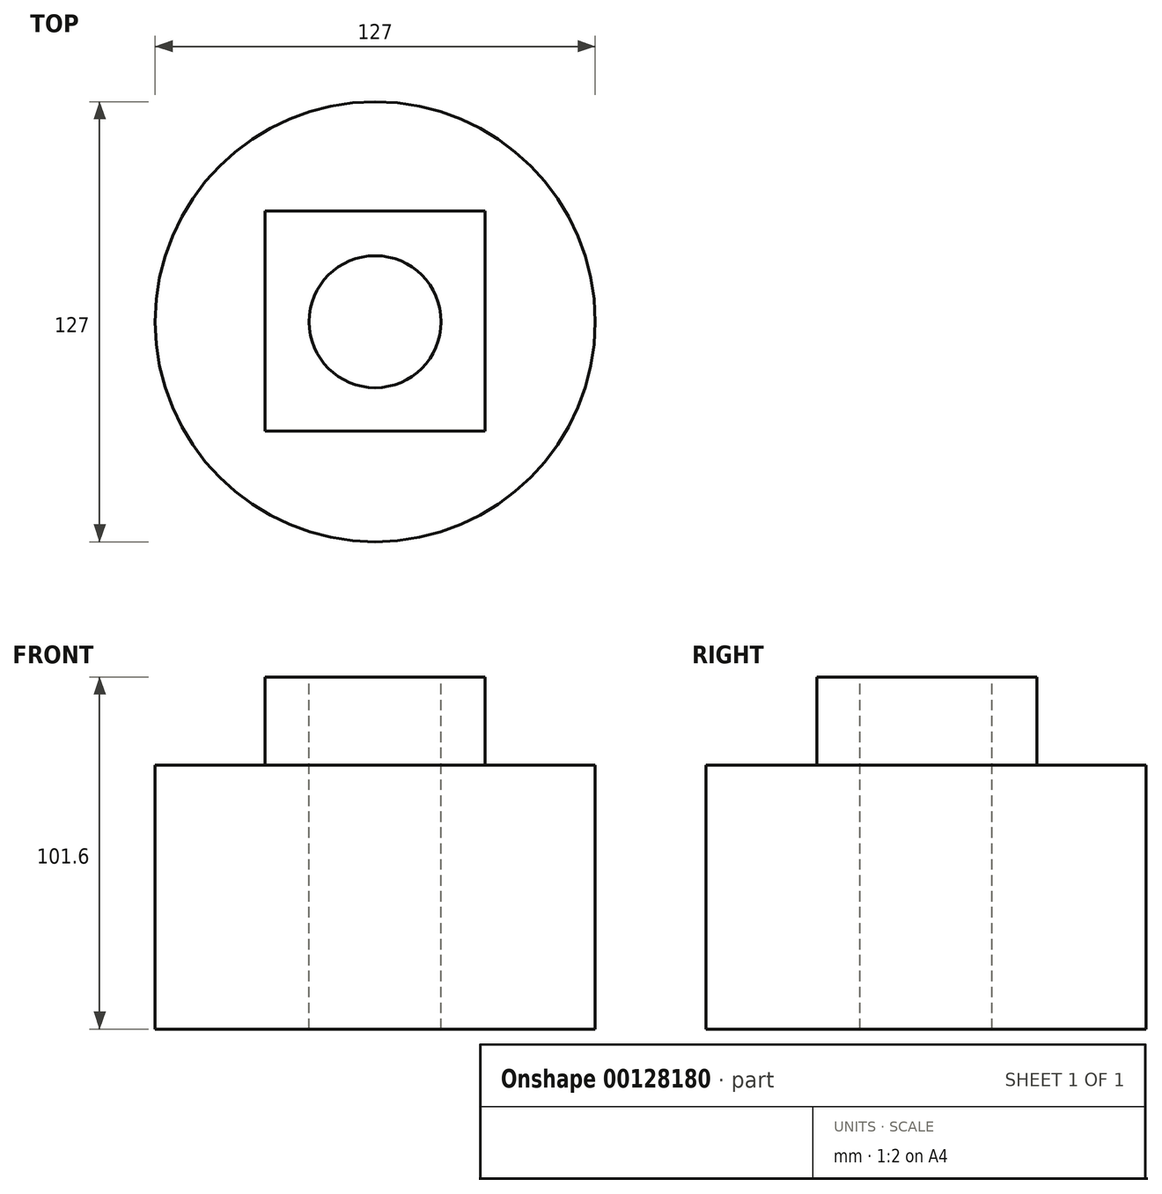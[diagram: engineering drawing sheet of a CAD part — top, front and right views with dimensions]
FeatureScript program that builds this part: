
annotation { "Feature Type Name" : "Feature", "Feature Type Description" : "" }
export const myFeature = defineFeature(function(context is Context, id is Id, definition is map)
    precondition{}
    {
        {
            var Q0;
            Q0=qCreatedBy(makeId("Top.planeOp"),FACE);
            cPlane(context, id + "F0", {"entities" : qUnion([Q0]), "cplaneType" : CPlaneType.OFFSET, "offset" : 25.4 * mm, "width" : 152.4 * mm, "height" : 152.4 * mm});
        }
        {
            var Q0;
            Q0=qCreatedBy(id+"F0.planeOp",FACE);
            var sketch = newSketch(context, id + "F1", { "sketchPlane" : qUnion([Q0])});
            skCircle(sketch, "E0", {"center": v(0, 0) * mm, "radius": 19.05 * mm});
            skLineSegment(sketch, "E1.bottom", {"start": v(-31.75, 31.75) * mm, "end": v(31.75, 31.75) * mm});
            skLineSegment(sketch, "E1.top", {"start": v(-31.75, -31.75) * mm, "end": v(31.75, -31.75) * mm});
            skLineSegment(sketch, "E1.left", {"start": v(-31.75, 31.75) * mm, "end": v(-31.75, -31.75) * mm});
            skLineSegment(sketch, "E1.right", {"start": v(31.75, 31.75) * mm, "end": v(31.75, -31.75) * mm});
            skSolve(sketch);
        }
        {
            var Q0;
            Q0=qCreatedBy(makeId("Top.planeOp"),FACE);
            var sketch = newSketch(context, id + "F2", { "sketchPlane" : qUnion([Q0])});
            skCircle(sketch, "E2", {"center": v(0, 0) * mm, "radius": 63.5 * mm});
            skSolve(sketch);
        }
        {
            var Q0;
            Q0=qCreatedBy(makeId("Right.planeOp"),FACE);
            var sketch = newSketch(context, id + "F3", { "sketchPlane" : qUnion([Q0])});
            skLineSegment(sketch, "E3.bottom", {"start": v(31.92, 25.4) * mm, "end": v(-31.58, 25.4) * mm});
            skLineSegment(sketch, "E3.top", {"start": v(31.92, 0) * mm, "end": v(-31.58, 0) * mm});
            skLineSegment(sketch, "E3.left", {"start": v(31.92, 25.4) * mm, "end": v(31.92, 0) * mm});
            skLineSegment(sketch, "E3.right", {"start": v(-31.58, 25.4) * mm, "end": v(-31.58, 0) * mm});
            skPoint(sketch, "E4.0", {"position": v(0, 0) * mm});
            skSolve(sketch);
        }
        {
            var Q0;
            Q0=makeQuery(id+"F3.imprint","IMPRINT",FACE,{"disambiguationData":[TD([[makeQuery(id+"F3.imprint","IMPRINT",EDGE,{"derivedFrom":sQuery(id+"F3.wireOp",EDGE,"E3.bottom")}),1.0]])]});
            extrude(context, id + "F4", {"entities" : qUnion([Q0]), "depth" : 31.75 * mm});
        }
        {
            var Q0;
            Q0=makeQuery(id+"F4.opExtrude","CAP_FACE",FACE,{"disambiguationData":[OSD([sQuery(id+"F3.wireOp",EDGE,"E3.bottom"),sQuery(id+"F3.wireOp",EDGE,"E3.top"),sQuery(id+"F3.wireOp",EDGE,"E3.left"),sQuery(id+"F3.wireOp",EDGE,"E3.right")])],"isStart":true});
            extrude(context, id + "F5", {"entities" : qUnion([Q0]), "operationType" : NewBodyOperationType.ADD, "depth" : 31.75 * mm});
        }
        {
            var Q0;
            Q0=makeQuery(id+"F2.imprint","IMPRINT",FACE,{"disambiguationData":[TD([[makeQuery(id+"F2.imprint","IMPRINT",EDGE,{"derivedFrom":sQuery(id+"F2.wireOp",EDGE,"E2")}),1.0]])]});
            extrude(context, id + "F6", {"entities" : qUnion([Q0]), "operationType" : NewBodyOperationType.ADD, "oppositeDirection" : true, "depth" : 76.2 * mm});
        }
        {
            var Q0;
            Q0=sQuery(id+"F1.wireOp",VERTEX,"E0.center");
            var Q1;
            Q1=makeQuery(id+"F4.opExtrude","SWEPT_BODY",BODY,{"disambiguationData":[OSD([sQuery(id+"F3.wireOp",EDGE,"E3.bottom"),sQuery(id+"F3.wireOp",EDGE,"E3.top"),sQuery(id+"F3.wireOp",EDGE,"E3.left"),sQuery(id+"F3.wireOp",EDGE,"E3.right")])]});
            hole(context, id + "F7", {"style" : HoleStyle.SIMPLE, "endStyle" : HoleEndStyle.THROUGH, "holeDiameter" : 38.1 * mm, "locations" : qUnion([Q0]), "scope" : qUnion([Q1]), "isTappedThrough" : true});
        }
    });
